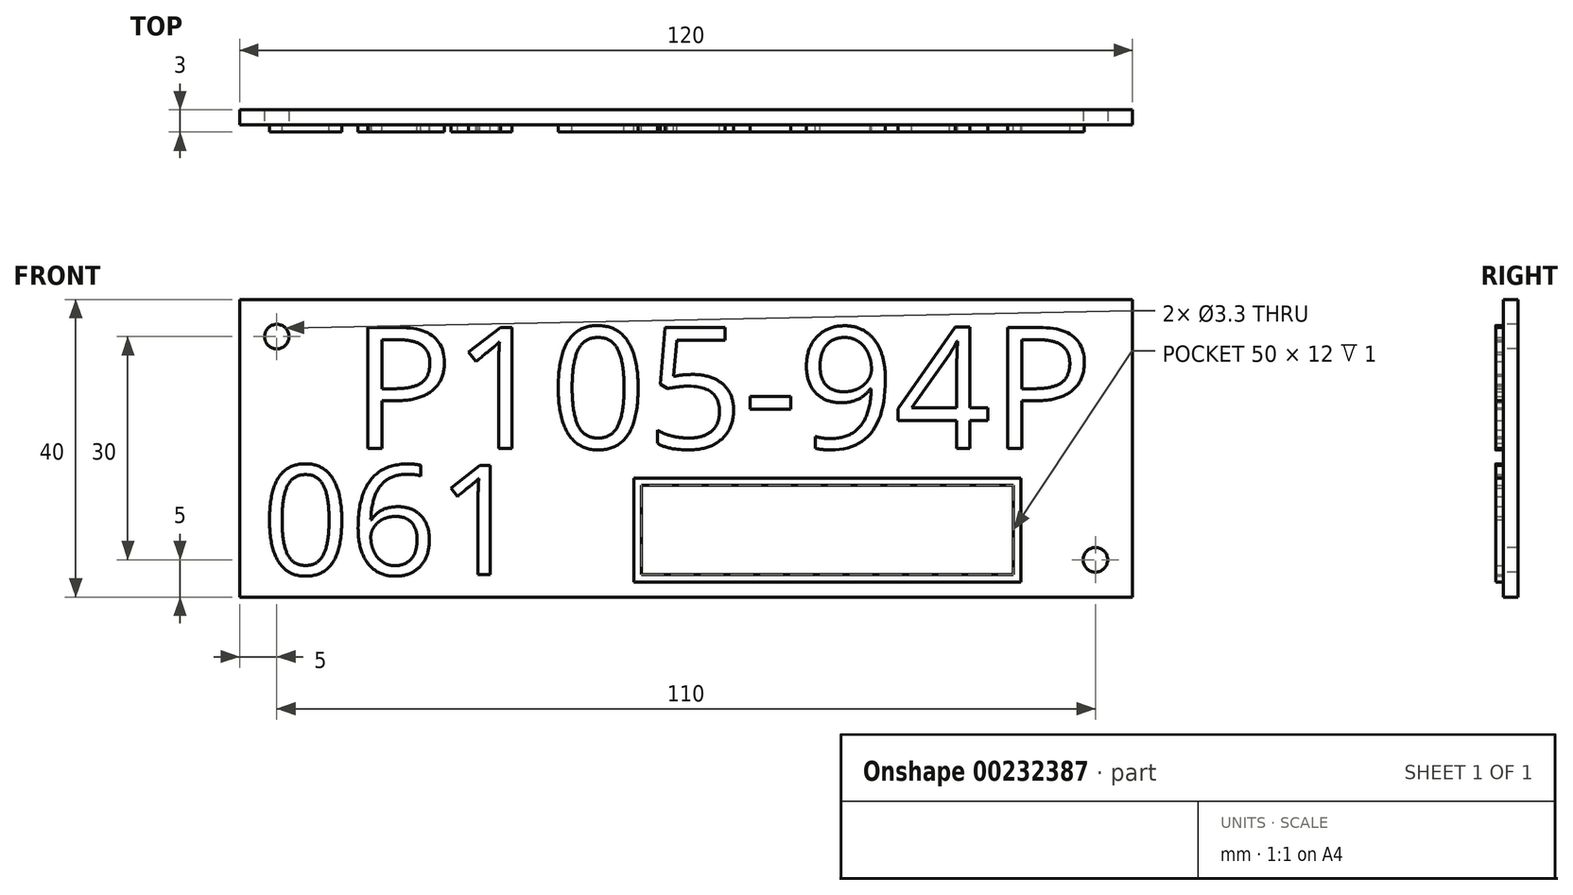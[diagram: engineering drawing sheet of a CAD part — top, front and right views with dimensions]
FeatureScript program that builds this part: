
annotation { "Feature Type Name" : "Feature", "Feature Type Description" : "" }
export const myFeature = defineFeature(function(context is Context, id is Id, definition is map)
    precondition{}
    {
        {
            var Q0;
            Q0=qCreatedBy(makeId("Front.planeOp"),FACE);
            var sketch = newSketch(context, id + "F0", { "sketchPlane" : qUnion([Q0])});
            skLineSegment(sketch, "E0.bottom", {"start": v(60, -20) * mm, "end": v(-60, -20) * mm});
            skLineSegment(sketch, "E0.top", {"start": v(60, 20) * mm, "end": v(-60, 20) * mm});
            skLineSegment(sketch, "E0.left", {"start": v(60, -20) * mm, "end": v(60, 20) * mm});
            skLineSegment(sketch, "E0.right", {"start": v(-60, -20) * mm, "end": v(-60, 20) * mm});
            skPoint(sketch, "E0.middle", {"position": v(0, 0) * mm});
            skSolve(sketch);
        }
        {
            var Q0;
            Q0=makeQuery(id+"F0.imprint","IMPRINT",FACE,{"disambiguationData":[TD([[makeQuery(id+"F0.imprint","IMPRINT",EDGE,{"derivedFrom":sQuery(id+"F0.wireOp",EDGE,"E0.bottom")}),-1.0]])]});
            extrude(context, id + "F1", {"entities" : qUnion([Q0]), "depth" : 2 * mm});
        }
        {
            var Q0;
            Q0=makeQuery(id+"F1.opExtrude","CAP_FACE",FACE,{"disambiguationData":[OSD([sQuery(id+"F0.wireOp",EDGE,"E0.bottom"),sQuery(id+"F0.wireOp",EDGE,"E0.top"),sQuery(id+"F0.wireOp",EDGE,"E0.left"),sQuery(id+"F0.wireOp",EDGE,"E0.right")])],"isStart":false});
            var sketch = newSketch(context, id + "F2", { "sketchPlane" : qUnion([Q0])});
            skPoint(sketch, "E1", {"position": v(-55, 15) * mm});
            skPoint(sketch, "E2", {"position": v(55, -15) * mm});
            skSolve(sketch);
        }
        {
            var Q0;
            Q0=sQuery(id+"F2.wireOp",VERTEX,"E1");
            var Q1;
            Q1=sQuery(id+"F2.wireOp",VERTEX,"E2");
            var Q2;
            Q2=makeQuery(id+"F1.opExtrude","SWEPT_BODY",BODY,{"disambiguationData":[OSD([sQuery(id+"F0.wireOp",EDGE,"E0.bottom"),sQuery(id+"F0.wireOp",EDGE,"E0.top"),sQuery(id+"F0.wireOp",EDGE,"E0.left"),sQuery(id+"F0.wireOp",EDGE,"E0.right")])]});
            hole(context, id + "F3", {"style" : HoleStyle.SIMPLE, "endStyle" : HoleEndStyle.THROUGH, "holeDiameter" : 3.3 * mm, "locations" : qUnion([Q0, Q1]), "scope" : qUnion([Q2]), "isTappedThrough" : true});
        }
        {
            var Q0;
            Q0=makeQuery(id+"F1.opExtrude","CAP_FACE",FACE,{"disambiguationData":[OSD([sQuery(id+"F0.wireOp",EDGE,"E0.bottom"),sQuery(id+"F0.wireOp",EDGE,"E0.top"),sQuery(id+"F0.wireOp",EDGE,"E0.left"),sQuery(id+"F0.wireOp",EDGE,"E0.right")])],"isStart":false});
            var sketch = newSketch(context, id + "F4", { "sketchPlane" : qUnion([Q0])});
            skText(sketch, "E3", { "text": "P105-94P", "fontName": "OpenSans-Regular.ttf"});
            const initialGuessF4  = {"E3": [-0.045, 0, 1, 0, 0.01637]};
            skSetInitialGuess(sketch, initialGuessF4);
            skSolve(sketch);
        }
        {
            var Q0;
            Q0=qSketchRegion(id+"F4",true);
            extrude(context, id + "F5", {"entities" : qUnion([Q0]), "operationType" : NewBodyOperationType.ADD, "depth" : 1 * mm});
        }
        {
            var Q0;
            {var subQ0=sQuery(id+"F0.wireOp",EDGE,"E0.top");var subQ1=sQuery(id+"F0.wireOp",EDGE,"E0.left");var subQ2=sQuery(id+"F0.wireOp",EDGE,"E0.right");var subQ3=sQuery(id+"F0.wireOp",EDGE,"E0.bottom");Q0=makeQuery(id+"F5.boolean.opBoolean","SPLIT",FACE,{"disambiguationData":[TD([makeQuery(id+"F1.opExtrude","SWEPT_FACE",FACE,{"disambiguationData":[OSD([subQ3])]})])],"derivedFrom":makeQuery(id+"F1.opExtrude","CAP_FACE",FACE,{"disambiguationData":[OSD([subQ3,subQ0,subQ1,subQ2])],"isStart":false})});}
            var sketch = newSketch(context, id + "F6", { "sketchPlane" : qUnion([Q0])});
            skText(sketch, "E4", { "text": "061", "fontName": "OpenSans-Regular.ttf"});
            const initialGuessF6  = {"E4": [-0.057, -0.017, 1, 0, 0.0148]};
            skSetInitialGuess(sketch, initialGuessF6);
            skSolve(sketch);
        }
        {
            var Q0;
            Q0=qSketchRegion(id+"F6",true);
            extrude(context, id + "F7", {"entities" : qUnion([Q0]), "operationType" : NewBodyOperationType.ADD, "depth" : 1 * mm});
        }
        {
            var Q0;
            {var subQ46=sQuery(id+"F0.wireOp",EDGE,"E0.top");var subQ48=sQuery(id+"F0.wireOp",EDGE,"E0.left");var subQ66=sQuery(id+"F0.wireOp",EDGE,"E0.right");var subQ76=sQuery(id+"F0.wireOp",EDGE,"E0.bottom");var subQ77=makeQuery(id+"F1.opExtrude","SWEPT_FACE",FACE,{"disambiguationData":[OSD([subQ76])]});Q0=makeQuery(id+"F7.boolean.opBoolean","SPLIT",FACE,{"disambiguationData":[TD([subQ77])],"derivedFrom":makeQuery(id+"F5.boolean.opBoolean","SPLIT",FACE,{"disambiguationData":[TD([subQ77])],"derivedFrom":makeQuery(id+"F1.opExtrude","CAP_FACE",FACE,{"disambiguationData":[OSD([subQ76,subQ46,subQ48,subQ66])],"isStart":false})})});}
            var sketch = newSketch(context, id + "F8", { "sketchPlane" : qUnion([Q0])});
            skLineSegment(sketch, "E5.bottom", {"start": v(45, -18) * mm, "end": v(-7, -18) * mm});
            skLineSegment(sketch, "E5.top", {"start": v(45, -4) * mm, "end": v(-7, -4) * mm});
            skLineSegment(sketch, "E5.left", {"start": v(45, -18) * mm, "end": v(45, -4) * mm});
            skLineSegment(sketch, "E5.right", {"start": v(-7, -18) * mm, "end": v(-7, -4) * mm});
            skPoint(sketch, "E5.middle", {"position": v(19, -11) * mm});
            skLineSegment(sketch, "E6.0", {"start": v(44, -5) * mm, "end": v(-6, -5) * mm});
            skLineSegment(sketch, "E6.1", {"start": v(44, -17) * mm, "end": v(44, -5) * mm});
            skLineSegment(sketch, "E6.2", {"start": v(44, -17) * mm, "end": v(-6, -17) * mm});
            skLineSegment(sketch, "E6.3", {"start": v(-6, -17) * mm, "end": v(-6, -5) * mm});
            skSolve(sketch);
        }
        {
            var Q0;
            Q0=makeQuery(id+"F8.imprint","IMPRINT",FACE,{"disambiguationData":[TD([[makeQuery(id+"F8.imprint","IMPRINT",EDGE,{"derivedFrom":sQuery(id+"F8.wireOp",EDGE,"E5.bottom")}),-1.0]])]});
            extrude(context, id + "F9", {"entities" : qUnion([Q0]), "operationType" : NewBodyOperationType.ADD, "depth" : 1 * mm});
        }
    });
